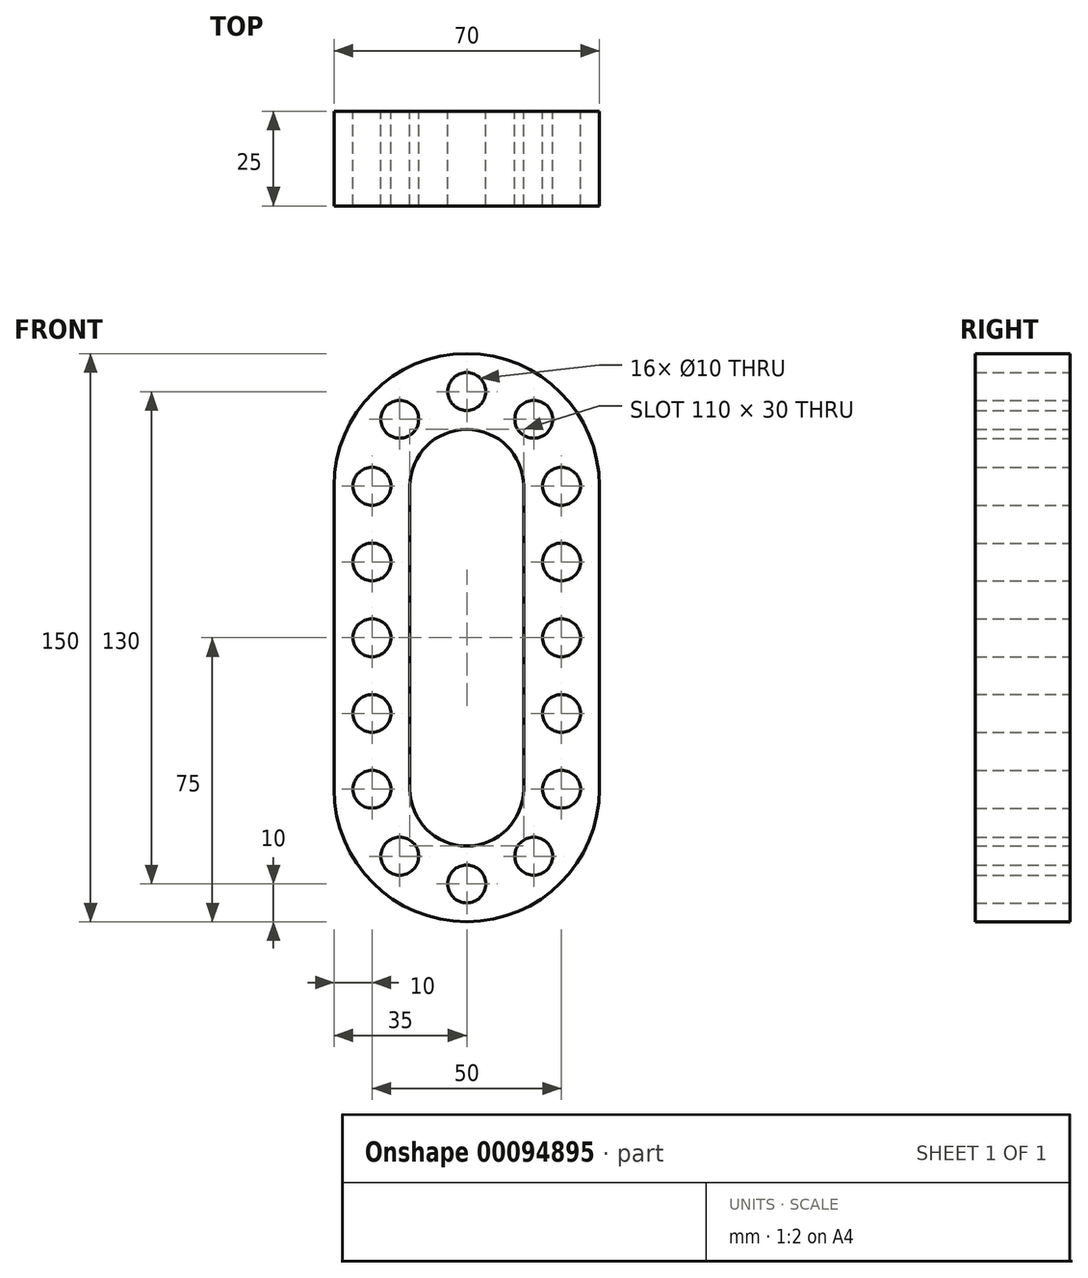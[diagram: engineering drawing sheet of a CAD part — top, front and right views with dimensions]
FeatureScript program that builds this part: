
annotation { "Feature Type Name" : "Feature", "Feature Type Description" : "" }
export const myFeature = defineFeature(function(context is Context, id is Id, definition is map)
    precondition{}
    {
        {
            var Q0;
            Q0=qCreatedBy(makeId("Front.planeOp"),FACE);
            var sketch = newSketch(context, id + "F0", { "sketchPlane" : qUnion([Q0])});
            skArc(sketch, "E0", {"start": v(0, 55) * mm, "mid": v(-10.6, 50.6) * mm, "end": v(-15, 40) * mm});
            skLineSegment(sketch, "E1", {"start": v(-15, 40) * mm, "end": v(-15, 0) * mm});
            skLineSegment(sketch, "E2.0", {"start": v(-35, 40) * mm, "end": v(-35, 0) * mm});
            skArc(sketch, "E2.1", {"start": v(0, 75) * mm, "mid": v(-24.75, 64.75) * mm, "end": v(-35, 40) * mm});
            skLineSegment(sketch, "E3", {"start": v(-35, 40) * mm, "end": v(43.7, 40) * mm, "construction": true});
            skCircle(sketch, "E4", {"center": v(-25, 40) * mm, "radius": 5 * mm});
            skCircle(sketch, "E5.1.0", {"center": v(-17.68, 57.68) * mm, "radius": 5 * mm});
            skCircle(sketch, "E5.2.0", {"center": v(0, 65) * mm, "radius": 5 * mm});
            skLineSegment(sketch, "E5.anchor1", {"start": v(0, 40) * mm, "end": v(-25, 40) * mm, "construction": true});
            skLineSegment(sketch, "E5.anchor2", {"start": v(0, 40) * mm, "end": v(0, 65) * mm, "construction": true});
            skCircle(sketch, "E6", {"center": v(-25, 0) * mm, "radius": 5 * mm});
            skCircle(sketch, "E7", {"center": v(-25, 20) * mm, "radius": 5 * mm});
            skLineSegment(sketch, "E8.MirrorCS", {"start": v(15, 40) * mm, "end": v(15, 0) * mm});
            skLineSegment(sketch, "E9.MirrorCS", {"start": v(35, 40) * mm, "end": v(35, 0) * mm});
            skCircle(sketch, "E10.MirrorC", {"center": v(25, 20) * mm, "radius": 5 * mm});
            skCircle(sketch, "E11.MirrorC", {"center": v(25, 40) * mm, "radius": 5 * mm});
            skCircle(sketch, "E12.MirrorC", {"center": v(17.68, 57.68) * mm, "radius": 5 * mm});
            skArc(sketch, "E13.MirrorCS", {"start": v(0, 55) * mm, "mid": v(10.6, 50.6) * mm, "end": v(15, 40) * mm});
            skArc(sketch, "E14.MirrorCS", {"start": v(0, 75) * mm, "mid": v(24.75, 64.75) * mm, "end": v(35, 40) * mm});
            skCircle(sketch, "E15.MirrorC", {"center": v(25, 0) * mm, "radius": 5 * mm});
            skLineSegment(sketch, "E16.MirrorCS", {"start": v(-15, -40) * mm, "end": v(-15, 0) * mm});
            skLineSegment(sketch, "E17.MirrorCS", {"start": v(-35, -40) * mm, "end": v(-35, 0) * mm});
            skCircle(sketch, "E18.MirrorC", {"center": v(-25, -20) * mm, "radius": 5 * mm});
            skCircle(sketch, "E19.MirrorC", {"center": v(-25, -40) * mm, "radius": 5 * mm});
            skCircle(sketch, "E20.MirrorC", {"center": v(-17.68, -57.68) * mm, "radius": 5 * mm});
            skCircle(sketch, "E21.MirrorC", {"center": v(0, -65) * mm, "radius": 5 * mm});
            skArc(sketch, "E22.MirrorCS", {"start": v(0, -55) * mm, "mid": v(-10.6, -50.6) * mm, "end": v(-15, -40) * mm});
            skArc(sketch, "E23.MirrorCS", {"start": v(0, -75) * mm, "mid": v(-24.75, -64.75) * mm, "end": v(-35, -40) * mm});
            skArc(sketch, "E24.MirrorCS", {"start": v(0, -55) * mm, "mid": v(10.6, -50.6) * mm, "end": v(15, -40) * mm});
            skLineSegment(sketch, "E25.MirrorCS", {"start": v(15, -40) * mm, "end": v(15, 0) * mm});
            skLineSegment(sketch, "E26.MirrorCS", {"start": v(35, -40) * mm, "end": v(35, 0) * mm});
            skCircle(sketch, "E27.MirrorC", {"center": v(25, -20) * mm, "radius": 5 * mm});
            skCircle(sketch, "E28.MirrorC", {"center": v(25, -40) * mm, "radius": 5 * mm});
            skCircle(sketch, "E29.MirrorC", {"center": v(17.68, -57.68) * mm, "radius": 5 * mm});
            skArc(sketch, "E30.MirrorCS", {"start": v(0, -75) * mm, "mid": v(24.75, -64.75) * mm, "end": v(35, -40) * mm});
            skSolve(sketch);
        }
        {
            var Q0;
            Q0 = qSketchRegion(id + "F0", true);
            extrude(context, id + "F1", {"entities" : qUnion([Q0]), "depth" : 25 * mm});
        }
    });
